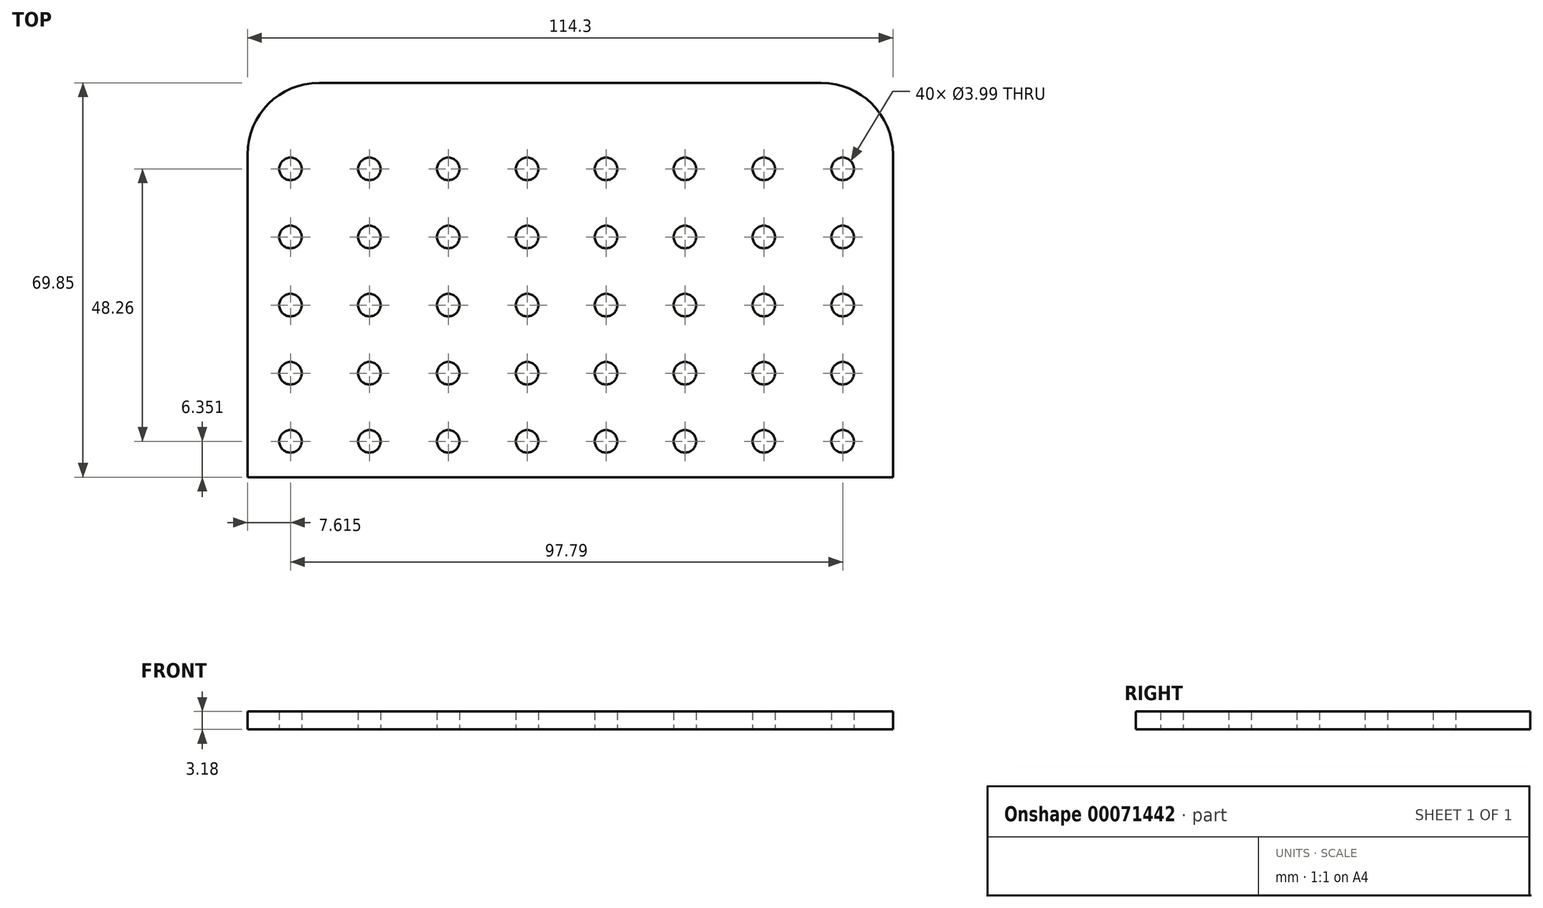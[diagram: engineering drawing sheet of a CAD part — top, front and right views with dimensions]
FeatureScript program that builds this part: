
annotation { "Feature Type Name" : "Feature", "Feature Type Description" : "" }
export const myFeature = defineFeature(function(context is Context, id is Id, definition is map)
    precondition{}
    {
        {
            var Q0;
            Q0=qCreatedBy(makeId("Top.planeOp"),FACE);
            var sketch = newSketch(context, id + "F0", { "sketchPlane" : qUnion([Q0])});
            skLineSegment(sketch, "E0.bottom", {"start": v(-41.28, 43.88) * mm, "end": v(47.62, 43.88) * mm});
            skLineSegment(sketch, "E0.top", {"start": v(-53.98, -25.97) * mm, "end": v(60.32, -25.97) * mm});
            skLineSegment(sketch, "E0.left", {"start": v(-53.98, 31.18) * mm, "end": v(-53.98, -25.97) * mm});
            skLineSegment(sketch, "E0.right", {"start": v(60.32, 31.18) * mm, "end": v(60.32, -25.97) * mm});
            skPoint(sketch, "E1.visualSharp", {"position": v(-53.98, 43.88) * mm});
            skArc(sketch, "E1.filletArc", {"start": v(-41.28, 43.88) * mm, "mid": v(-50.27, 40.16) * mm, "end": v(-53.98, 31.18) * mm});
            skPoint(sketch, "E2.visualSharp", {"position": v(60.32, 43.88) * mm});
            skArc(sketch, "E2.filletArc", {"start": v(60.32, 31.18) * mm, "mid": v(56.6, 40.16) * mm, "end": v(47.62, 43.88) * mm});
            skCircle(sketch, "E3", {"center": v(-46.36, -19.62) * mm, "radius": 2 * mm});
            skCircle(sketch, "E4.0.1.0", {"center": v(-46.36, -7.55) * mm, "radius": 2 * mm});
            skCircle(sketch, "E4.0.2.0", {"center": v(-46.36, 4.51) * mm, "radius": 2 * mm});
            skCircle(sketch, "E4.0.3.0", {"center": v(-46.36, 16.58) * mm, "radius": 2 * mm});
            skCircle(sketch, "E4.0.4.0", {"center": v(-46.36, 28.64) * mm, "radius": 2 * mm});
            skCircle(sketch, "E4.1.0.0", {"center": v(-32.4, -19.62) * mm, "radius": 2 * mm});
            skCircle(sketch, "E4.1.1.0", {"center": v(-32.4, -7.55) * mm, "radius": 2 * mm});
            skCircle(sketch, "E4.1.2.0", {"center": v(-32.4, 4.51) * mm, "radius": 2 * mm});
            skCircle(sketch, "E4.1.3.0", {"center": v(-32.4, 16.58) * mm, "radius": 2 * mm});
            skCircle(sketch, "E4.1.4.0", {"center": v(-32.4, 28.64) * mm, "radius": 2 * mm});
            skCircle(sketch, "E4.2.0.0", {"center": v(-18.42, -19.62) * mm, "radius": 2 * mm});
            skCircle(sketch, "E4.2.1.0", {"center": v(-18.42, -7.55) * mm, "radius": 2 * mm});
            skCircle(sketch, "E4.2.2.0", {"center": v(-18.42, 4.51) * mm, "radius": 2 * mm});
            skCircle(sketch, "E4.2.3.0", {"center": v(-18.42, 16.58) * mm, "radius": 2 * mm});
            skCircle(sketch, "E4.2.4.0", {"center": v(-18.42, 28.64) * mm, "radius": 2 * mm});
            skCircle(sketch, "E4.3.0.0", {"center": v(-4.45, -19.62) * mm, "radius": 2 * mm});
            skCircle(sketch, "E4.3.1.0", {"center": v(-4.45, -7.55) * mm, "radius": 2 * mm});
            skCircle(sketch, "E4.3.2.0", {"center": v(-4.45, 4.51) * mm, "radius": 2 * mm});
            skCircle(sketch, "E4.3.3.0", {"center": v(-4.45, 16.58) * mm, "radius": 2 * mm});
            skCircle(sketch, "E4.3.4.0", {"center": v(-4.45, 28.64) * mm, "radius": 2 * mm});
            skCircle(sketch, "E4.4.0.0", {"center": v(9.52, -19.62) * mm, "radius": 2 * mm});
            skCircle(sketch, "E4.4.1.0", {"center": v(9.52, -7.55) * mm, "radius": 2 * mm});
            skCircle(sketch, "E4.4.2.0", {"center": v(9.52, 4.51) * mm, "radius": 2 * mm});
            skCircle(sketch, "E4.4.3.0", {"center": v(9.52, 16.58) * mm, "radius": 2 * mm});
            skCircle(sketch, "E4.4.4.0", {"center": v(9.52, 28.64) * mm, "radius": 2 * mm});
            skCircle(sketch, "E4.5.0.0", {"center": v(23.49, -19.62) * mm, "radius": 2 * mm});
            skCircle(sketch, "E4.5.1.0", {"center": v(23.49, -7.55) * mm, "radius": 2 * mm});
            skCircle(sketch, "E4.5.2.0", {"center": v(23.49, 4.51) * mm, "radius": 2 * mm});
            skCircle(sketch, "E4.5.3.0", {"center": v(23.49, 16.58) * mm, "radius": 2 * mm});
            skCircle(sketch, "E4.5.4.0", {"center": v(23.49, 28.64) * mm, "radius": 2 * mm});
            skCircle(sketch, "E4.6.0.0", {"center": v(37.46, -19.62) * mm, "radius": 2 * mm});
            skCircle(sketch, "E4.6.1.0", {"center": v(37.46, -7.55) * mm, "radius": 2 * mm});
            skCircle(sketch, "E4.6.2.0", {"center": v(37.46, 4.51) * mm, "radius": 2 * mm});
            skCircle(sketch, "E4.6.3.0", {"center": v(37.46, 16.58) * mm, "radius": 2 * mm});
            skCircle(sketch, "E4.6.4.0", {"center": v(37.46, 28.64) * mm, "radius": 2 * mm});
            skCircle(sketch, "E4.7.0.0", {"center": v(51.43, -19.62) * mm, "radius": 2 * mm});
            skCircle(sketch, "E4.7.1.0", {"center": v(51.43, -7.55) * mm, "radius": 2 * mm});
            skCircle(sketch, "E4.7.2.0", {"center": v(51.43, 4.51) * mm, "radius": 2 * mm});
            skCircle(sketch, "E4.7.3.0", {"center": v(51.43, 16.58) * mm, "radius": 2 * mm});
            skCircle(sketch, "E4.7.4.0", {"center": v(51.43, 28.64) * mm, "radius": 2 * mm});
            skSolve(sketch);
        }
        {
            var Q0;
            Q0=makeQuery(id+"F0.imprint","IMPRINT",FACE,{"disambiguationData":[TD([[makeQuery(id+"F0.imprint","IMPRINT",EDGE,{"derivedFrom":sQuery(id+"F0.wireOp",EDGE,"E0.bottom")}),-1.0]])]});
            extrude(context, id + "F1", {"entities" : qUnion([Q0]), "depth" : 3.17 * mm, "offsetDistance" : 25.4 * mm});
        }
    });
